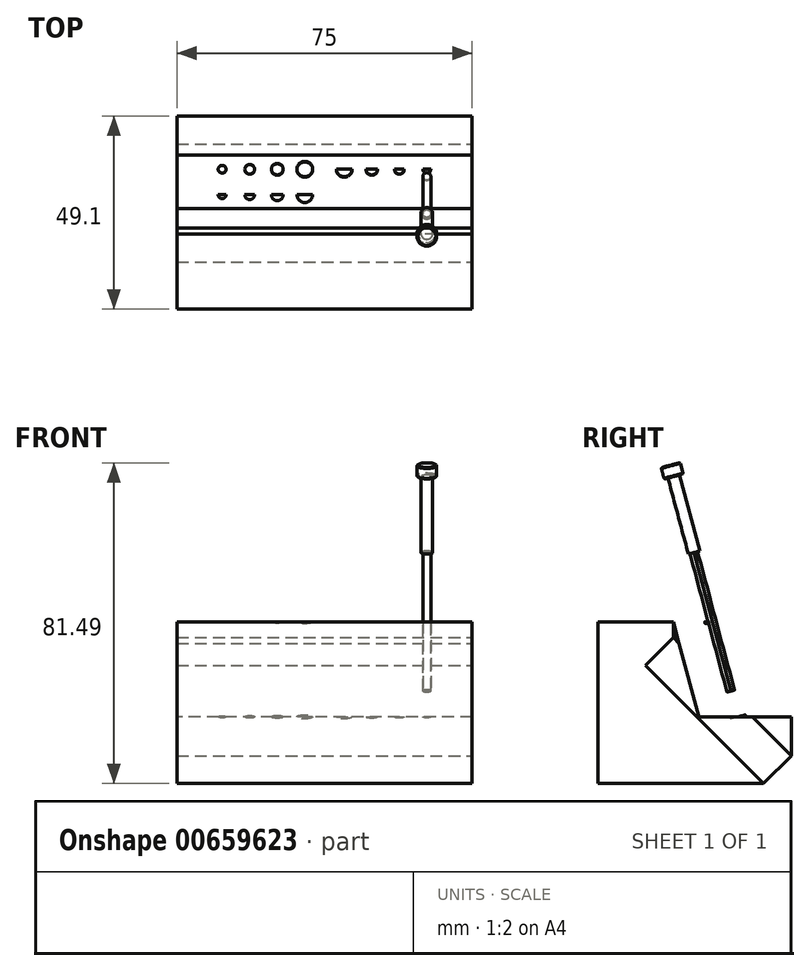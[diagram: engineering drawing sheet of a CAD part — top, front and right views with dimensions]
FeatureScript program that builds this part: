
annotation { "Feature Type Name" : "Feature", "Feature Type Description" : "" }
export const myFeature = defineFeature(function(context is Context, id is Id, definition is map)
    precondition{}
    {
        {
            var Q0;
            Q0=qCreatedBy(makeId("Top.planeOp"),FACE);
            var sketch = newSketch(context, id + "F0", { "sketchPlane" : qUnion([Q0])});
            skLineSegment(sketch, "E0.bottom", {"start": v(37.5, -15) * mm, "end": v(-37.5, -15) * mm});
            skLineSegment(sketch, "E0.top", {"start": v(37.5, 15) * mm, "end": v(-37.5, 15) * mm});
            skLineSegment(sketch, "E0.left", {"start": v(37.5, -15) * mm, "end": v(37.5, 15) * mm});
            skLineSegment(sketch, "E0.right", {"start": v(-37.5, -15) * mm, "end": v(-37.5, 15) * mm});
            skPoint(sketch, "E0.middle", {"position": v(0, 0) * mm});
            skSolve(sketch);
        }
        {
            var Q0;
            Q0=makeQuery(id+"F0.imprint","IMPRINT",FACE,{"disambiguationData":[TD([[makeQuery(id+"F0.imprint","IMPRINT",EDGE,{"derivedFrom":sQuery(id+"F0.wireOp",EDGE,"E0.bottom")}),-1.0]])]});
            extrude(context, id + "F1", {"entities" : qUnion([Q0]), "oppositeDirection" : true, "depth" : 50 * mm, "offsetDistance" : 25 * mm});
        }
        {
            var Q0;
            Q0=makeQuery(id+"F1.opExtrude","SWEPT_FACE",FACE,{"disambiguationData":[OSD([sQuery(id+"F0.wireOp",EDGE,"E0.left")])]});
            var sketch = newSketch(context, id + "F2", { "sketchPlane" : qUnion([Q0])});
            skLineSegment(sketch, "E1", {"start": v(-15, -4.02) * mm, "end": v(15, -34.02) * mm});
            skLineSegment(sketch, "E2.0", {"start": v(-15, -50) * mm, "end": v(-15, -4.02) * mm});
            skPoint(sketch, "E3.orphan", {"position": v(-14.02, -5) * mm});
            skPoint(sketch, "E4.orphan", {"position": v(15, -50) * mm});
            skLineSegment(sketch, "E5", {"start": v(15, -34.02) * mm, "end": v(15, -50) * mm});
            skPoint(sketch, "E6.0.end.orphan", {"position": v(15, 0) * mm});
            skPoint(sketch, "E7.orphan", {"position": v(-15, 0) * mm});
            skLineSegment(sketch, "E8.0", {"start": v(-15, -50) * mm, "end": v(15, -50) * mm});
            skSolve(sketch);
        }
        {
            var Q0;
            Q0=makeQuery(id+"F2.imprint","IMPRINT",FACE,{"disambiguationData":[TD([[makeQuery(id+"F2.imprint","IMPRINT",EDGE,{"derivedFrom":sQuery(id+"F2.wireOp",EDGE,"E1")}),-1.0]])]});
            extrude(context, id + "F3", {"entities" : qUnion([Q0]), "operationType" : NewBodyOperationType.REMOVE, "endBound" : BoundingType.THROUGH_ALL, "oppositeDirection" : true, "depth" : 25 * mm, "offsetDistance" : 25 * mm});
        }
        {
            var Q0;
            Q0=makeQuery(id+"F1.opExtrude","CAP_FACE",FACE,{"disambiguationData":[OSD([sQuery(id+"F0.wireOp",EDGE,"E0.bottom"),sQuery(id+"F0.wireOp",EDGE,"E0.top"),sQuery(id+"F0.wireOp",EDGE,"E0.left"),sQuery(id+"F0.wireOp",EDGE,"E0.right")])],"isStart":true});
            var sketch = newSketch(context, id + "F4", { "sketchPlane" : qUnion([Q0])});
            skCircle(sketch, "E9", {"center": v(26, -5) * mm, "radius": 1 * mm});
            skCircle(sketch, "E10", {"center": v(19, -5) * mm, "radius": 1.25 * mm});
            skCircle(sketch, "E11", {"center": v(12, -5) * mm, "radius": 1.5 * mm});
            skCircle(sketch, "E12", {"center": v(5, -5) * mm, "radius": 2 * mm});
            skLineSegment(sketch, "E13", {"start": v(0, 0) * mm, "end": v(0, -28.55) * mm, "construction": true});
            skCircle(sketch, "E14.MirrorC", {"center": v(-26, -5) * mm, "radius": 1 * mm});
            skCircle(sketch, "E15.MirrorC", {"center": v(-19, -5) * mm, "radius": 1.25 * mm});
            skCircle(sketch, "E16.MirrorC", {"center": v(-12, -5) * mm, "radius": 1.5 * mm});
            skCircle(sketch, "E17.MirrorC", {"center": v(-5, -5) * mm, "radius": 2 * mm});
            skLineSegment(sketch, "E18", {"start": v(26, -5) * mm, "end": v(-26, -5) * mm, "construction": true});
            skSolve(sketch);
        }
        {
            var Q0;
            Q0=makeQuery(id+"F1.opExtrude","SWEPT_FACE",FACE,{"disambiguationData":[OSD([sQuery(id+"F0.wireOp",EDGE,"E0.left")])]});
            var sketch = newSketch(context, id + "F5", { "sketchPlane" : qUnion([Q0])});
            skLineSegment(sketch, "E19.0", {"start": v(-15, -4.02) * mm, "end": v(15, -34.02) * mm});
            skLineSegment(sketch, "E20.0", {"start": v(-22.07, -11.1) * mm, "end": v(7.93, -41.1) * mm});
            skLineSegment(sketch, "E21", {"start": v(15, -34.02) * mm, "end": v(7.93, -41.1) * mm});
            skLineSegment(sketch, "E22", {"start": v(-15, -4.02) * mm, "end": v(-22.07, -11.1) * mm});
            skSolve(sketch);
        }
        {
            var Q0;
            Q0=makeQuery(id+"F5.imprint","IMPRINT",FACE,{"disambiguationData":[TD([[makeQuery(id+"F5.imprint","IMPRINT",EDGE,{"derivedFrom":sQuery(id+"F5.wireOp",EDGE,"E19.0")}),-1.0]])]});
            var Q1;
            Q1=makeQuery(id+"F1.opExtrude","SWEPT_FACE",FACE,{"disambiguationData":[OSD([sQuery(id+"F0.wireOp",EDGE,"E0.right")])]});
            extrude(context, id + "F6", {"entities" : qUnion([Q0]), "endBound" : BoundingType.UP_TO_SURFACE, "oppositeDirection" : true, "depth" : 25 * mm, "endBoundEntityFace" : qUnion([Q1]), "offsetDistance" : 25 * mm});
        }
        {
            var Q0;
            Q0=makeQuery(id+"F1.opExtrude","SWEPT_FACE",FACE,{"disambiguationData":[OSD([sQuery(id+"F0.wireOp",EDGE,"E0.left")])]});
            var sketch = newSketch(context, id + "F7", { "sketchPlane" : qUnion([Q0])});
            skLineSegment(sketch, "E23.0", {"start": v(-22.07, -11.1) * mm, "end": v(7.93, -41.1) * mm});
            skLineSegment(sketch, "E24", {"start": v(7.93, -41.1) * mm, "end": v(-34.1, -41.1) * mm});
            skLineSegment(sketch, "E25", {"start": v(-34.1, -41.1) * mm, "end": v(-34.1, 0) * mm});
            skLineSegment(sketch, "E26", {"start": v(-15, 0) * mm, "end": v(-34.1, 0) * mm});
            skLineSegment(sketch, "E27.0", {"start": v(-15, -4.02) * mm, "end": v(-22.07, -11.1) * mm});
            skSolve(sketch);
        }
        {
            var Q0;
            Q0=makeQuery(id+"F7.imprint","IMPRINT",FACE,{"disambiguationData":[TD([[makeQuery(id+"F7.imprint","IMPRINT",EDGE,{"derivedFrom":sQuery(id+"F7.wireOp",EDGE,"E23.0")}),-1.0]])]});
            var Q1;
            Q1=makeQuery(id+"F1.opExtrude","SWEPT_FACE",FACE,{"disambiguationData":[OSD([sQuery(id+"F0.wireOp",EDGE,"E0.right")])]});
            extrude(context, id + "F8", {"entities" : qUnion([Q0]), "endBound" : BoundingType.UP_TO_SURFACE, "oppositeDirection" : true, "depth" : 25 * mm, "endBoundEntityFace" : qUnion([Q1]), "offsetDistance" : 25 * mm});
        }
        {
            var Q0;
            Q0=sQuery(id+"F4.wireOp",EDGE,"E18");
            cPlane(context, id + "F9", {"entities" : qUnion([Q0]), "cplaneType" : CPlaneType.LINE_ANGLE, "offset" : 25 * mm, "angle" : 105 * degree, "oppositeDirection" : true, "width" : 150 * mm, "height" : 150 * mm});
        }
        {
            var Q0;
            Q0=qCreatedBy(id+"F9.planeOp",FACE);
            var sketch = newSketch(context, id + "F10", { "sketchPlane" : qUnion([Q0])});
            skEllipse(sketch, "E28.0", {"center": v(26, 4.83) * mm, "majorRadius": 1 * mm, "minorRadius": 0.98 * mm, "majorAxis": v(-1, 0)});
            skEllipse(sketch, "E29.0", {"center": v(19, 4.83) * mm, "majorRadius": 1.25 * mm, "minorRadius": 1.23 * mm, "majorAxis": v(-1, 0)});
            skEllipse(sketch, "E30.0", {"center": v(12, 4.83) * mm, "majorRadius": 1.5 * mm, "minorRadius": 1.48 * mm, "majorAxis": v(-1, 0)});
            skEllipse(sketch, "E31.0", {"center": v(5, 4.83) * mm, "majorRadius": 2 * mm, "minorRadius": 1.97 * mm, "majorAxis": v(-1, 0)});
            skEllipse(sketch, "E32.0", {"center": v(-5, 4.83) * mm, "majorRadius": 2 * mm, "minorRadius": 1.97 * mm, "majorAxis": v(1, 0)});
            skEllipse(sketch, "E33.0", {"center": v(-12, 4.83) * mm, "majorRadius": 1.5 * mm, "minorRadius": 1.48 * mm, "majorAxis": v(1, 0)});
            skEllipse(sketch, "E34.0", {"center": v(-19, 4.83) * mm, "majorRadius": 1.25 * mm, "minorRadius": 1.23 * mm, "majorAxis": v(1, 0)});
            skEllipse(sketch, "E35.0", {"center": v(-26, 4.83) * mm, "majorRadius": 1 * mm, "minorRadius": 0.98 * mm, "majorAxis": v(1, 0)});
            skSolve(sketch);
        }
        {
            var Q0;
            Q0 = qSketchRegion(id + "F10", true);
            var Q1;
            Q1=makeQuery(id+"F4.imprint","IMPRINT",FACE,{"disambiguationData":[TD([[makeQuery(id+"F4.imprint","IMPRINT",EDGE,{"derivedFrom":sQuery(id+"F4.wireOp",EDGE,"E9")}),1.0]])]});
            var Q2;
            Q2=makeQuery(id+"F4.imprint","IMPRINT",FACE,{"disambiguationData":[TD([[makeQuery(id+"F4.imprint","IMPRINT",EDGE,{"derivedFrom":sQuery(id+"F4.wireOp",EDGE,"E10")}),1.0]])]});
            var Q3;
            Q3=makeQuery(id+"F4.imprint","IMPRINT",FACE,{"disambiguationData":[TD([[makeQuery(id+"F4.imprint","IMPRINT",EDGE,{"derivedFrom":sQuery(id+"F4.wireOp",EDGE,"E11")}),1.0]])]});
            var Q4;
            Q4=makeQuery(id+"F4.imprint","IMPRINT",FACE,{"disambiguationData":[TD([[makeQuery(id+"F4.imprint","IMPRINT",EDGE,{"derivedFrom":sQuery(id+"F4.wireOp",EDGE,"E12")}),1.0]])]});
            var Q5;
            Q5=makeQuery(id+"F4.imprint","IMPRINT",FACE,{"disambiguationData":[TD([[makeQuery(id+"F4.imprint","IMPRINT",EDGE,{"derivedFrom":sQuery(id+"F4.wireOp",EDGE,"E17.MirrorC")}),-1.0]])]});
            var Q6;
            Q6=makeQuery(id+"F4.imprint","IMPRINT",FACE,{"disambiguationData":[TD([[makeQuery(id+"F4.imprint","IMPRINT",EDGE,{"derivedFrom":sQuery(id+"F4.wireOp",EDGE,"E16.MirrorC")}),-1.0]])]});
            var Q7;
            Q7=makeQuery(id+"F4.imprint","IMPRINT",FACE,{"disambiguationData":[TD([[makeQuery(id+"F4.imprint","IMPRINT",EDGE,{"derivedFrom":sQuery(id+"F4.wireOp",EDGE,"E15.MirrorC")}),-1.0]])]});
            var Q8;
            Q8=makeQuery(id+"F4.imprint","IMPRINT",FACE,{"disambiguationData":[TD([[makeQuery(id+"F4.imprint","IMPRINT",EDGE,{"derivedFrom":sQuery(id+"F4.wireOp",EDGE,"E14.MirrorC")}),-1.0]])]});
            extrude(context, id + "F11", {"entities" : qUnion([Q0, Q1, Q2, Q3, Q4, Q5, Q6, Q7, Q8]), "operationType" : NewBodyOperationType.REMOVE, "depth" : 25 * mm, "offsetDistance" : 25 * mm});
        }
        {
            var Q0;
            Q0=qCreatedBy(id+"F9.planeOp",FACE);
            var sketch = newSketch(context, id + "F12", { "sketchPlane" : qUnion([Q0])});
            skEllipticalArc(sketch, "E36.0", {});
            skFitSpline(sketch, "E37.0", {"points": [v(25, 4.92) * mm, v(25, 4.8) * mm, v(25.05, 4.54) * mm, v(25.27, 4.2) * mm, v(25.6, 4) * mm, v(26, 3.91) * mm, v(26.4, 4) * mm, v(26.73, 4.2) * mm, v(26.95, 4.54) * mm, v(27, 4.8) * mm, v(27, 4.92) * mm]});
            const initialGuessF12  = {"E36.0": [0.026, 0.004924038765061036, -1, 0, 0.001, 0.000984807753012208, 3.141592653589793, 0]};
            skSetInitialGuess(sketch, initialGuessF12);
            skSolve(sketch);
        }
        {
            var Q0;
            Q0 = qSketchRegion(id + "F12", true);
            extrude(context, id + "F13", {"entities" : qUnion([Q0]), "endBound" : BoundingType.SYMMETRIC, "depth" : 36.4 * mm, "offsetDistance" : 25 * mm});
        }
        {
            var Q0;
            Q0=makeQuery(id+"F13.opExtrude","CAP_FACE",FACE,{"disambiguationData":[OSD([sQuery(id+"F12.wireOp",EDGE,"E36.0"),sQuery(id+"F12.wireOp",EDGE,"E37.0")])],"isStart":false});
            chamfer(context, id + "F14", {"entities" : qUnion([Q0]), "width" : 0.05 * mm, "tangentPropagation" : true});
        }
        {
            var Q0;
            Q0=makeQuery(id+"F13.opExtrude","CAP_FACE",FACE,{"disambiguationData":[OSD([sQuery(id+"F12.wireOp",EDGE,"E36.0"),sQuery(id+"F12.wireOp",EDGE,"E37.0")])],"isStart":true});
            var sketch = newSketch(context, id + "F15", { "sketchPlane" : qUnion([Q0])});
            skCircle(sketch, "E38", {"center": v(26, -4.83) * mm, "radius": 1.5 * mm});
            skSolve(sketch);
        }
        {
            var Q0;
            Q0=makeQuery(id+"F15.imprint","IMPRINT",FACE,{"disambiguationData":[TD([[makeQuery(id+"F15.imprint","IMPRINT",EDGE,{"derivedFrom":sQuery(id+"F15.wireOp",EDGE,"E38")}),1.0]])]});
            var Q1;
            Q1=makeQuery(id+"F15.imprint","IMPRINT",FACE,{"disambiguationData":[TD([[makeQuery(id+"F15.imprint","IMPRINT",EDGE,{"derivedFrom":makeQuery(id+"F13.opExtrude","CAP_EDGE",EDGE,{"disambiguationData":[OSD([sQuery(id+"F12.wireOp",EDGE,"E36.0")])],"isStart":true})}),-1.0]])]});
            extrude(context, id + "F16", {"entities" : qUnion([Q0, Q1]), "operationType" : NewBodyOperationType.ADD, "depth" : 20 * mm, "offsetDistance" : 25 * mm});
        }
        {
            var Q0;
            Q0=makeQuery(id+"F16.opExtrude","CAP_FACE",FACE,{"disambiguationData":[OSD([sQuery(id+"F15.wireOp",EDGE,"E38")])],"isStart":false});
            var sketch = newSketch(context, id + "F17", { "sketchPlane" : qUnion([Q0])});
            skCircle(sketch, "E39", {"center": v(26, -4.83) * mm, "radius": 2.5 * mm});
            skSolve(sketch);
        }
        {
            var Q0;
            Q0=makeQuery(id+"F17.imprint","IMPRINT",FACE,{"disambiguationData":[TD([[makeQuery(id+"F17.imprint","IMPRINT",EDGE,{"derivedFrom":makeQuery(id+"F16.opExtrude","CAP_EDGE",EDGE,{"disambiguationData":[OSD([sQuery(id+"F15.wireOp",EDGE,"E38")])],"isStart":false})}),1.0]])]});
            var Q1;
            Q1=makeQuery(id+"F17.imprint","IMPRINT",FACE,{"disambiguationData":[TD([[makeQuery(id+"F17.imprint","IMPRINT",EDGE,{"derivedFrom":sQuery(id+"F17.wireOp",EDGE,"E39")}),1.0]])]});
            extrude(context, id + "F18", {"entities" : qUnion([Q0, Q1]), "operationType" : NewBodyOperationType.ADD, "depth" : 3 * mm, "offsetDistance" : 25 * mm});
        }
        {
            var Q0;
            Q0=makeQuery(id+"F18.opExtrude","CAP_EDGE",EDGE,{"disambiguationData":[OSD([sQuery(id+"F17.wireOp",EDGE,"E39")])],"isStart":false});
            var Q1;
            Q1=makeQuery(id+"F18.opExtrude","CAP_EDGE",EDGE,{"disambiguationData":[OSD([sQuery(id+"F17.wireOp",EDGE,"E39")])],"isStart":true});
            chamfer(context, id + "F19", {"entities" : qUnion([Q0, Q1]), "width" : .2 * mm, "tangentPropagation" : true});
        }
    });
